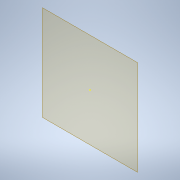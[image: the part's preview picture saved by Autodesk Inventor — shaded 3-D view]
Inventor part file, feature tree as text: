
AUTODESK INVENTOR PART (.ipt)
format: ipt  version: 2020 (Build 240168000, 168)  size: 429,568 bytes
history: native  units: in
note: dims shown in document units (in); Inventor stores cm internally (conversion verified against a paired STEP export)
features: sketch x12, extrude x8, projected_geometry x7, mirror x3, plane x2, other x2, fillet x1, reference x1
ambient origin geometry x8: Origin, YZ Plane, XZ Plane, XY Plane, X Axis, Y Axis, Z Axis, Center Point
bodies: Solid1 (feature_tree)
feature tree (36):
  sketch  "Sketch1"  dims[d0=0.5625in d1=0.0in d2=0.0625in d3=0.0in]
  extrude  "Extrusion1"  Depth=0.0625in TaperAngle=0.0deg
  extrude  "Extrusion2"  Depth=0.125in TaperAngle=0.0deg
  plane  "Work Plane1"
  mirror  "Mirror1"
  fillet  "Fillet1"  Radius=1.375in
  mirror  "Mirror2"
  sketch  "Sketch4"  dims[d12=-0.0625in d13=0.125in d14=0.0in]
  extrude  "Extrusion3"  Depth=1.375in TaperAngle=0.0deg
  extrude  "Extrusion4"  Depth=0.125in TaperAngle=0.0deg
  mirror  "Mirror3"
  extrude  "Extrusion5"  Depth=0.0625in TaperAngle=0.0deg
  sketch  "Sketch8"
  plane  "Work Plane2"
  extrude  "Extrusion6"  [1 undecoded]
  extrude  "Extrusion7"  [1 undecoded]
  sketch  "Sketch11"
  extrude  "Extrusion8"  [1 undecoded]
  sketch  "Sketch2"  dims[d4=0.125in d5=1.375in d6=0.0in d7=1.375in d8=0.0in]
  sketch  "Sketch3"  dims[d9=0.2843in d10=1.375in d11=0.0in]
  sketch  "Sketch5"  dims[d15=0.3125in d16=0.0in d17=0.0625in d18=0.0in]
  sketch  "Sketch6"
  projected_geometry  "Projected Loop1"
  sketch  "Sketch7"
  reference  "Reference1"
  projected_geometry  "Projected Loop2"
  projected_geometry  "Projected Loop3"
  sketch  "Sketch9"
  projected_geometry  "Projected Loop4"
  sketch  "Sketch10"
  projected_geometry  "Projected Loop5"
  sketch  "Sketch12"
  projected_geometry  "Projected Loop6"
  projected_geometry  "Project Cut Edges1"
  other  "Assembly1"
  other  "Micro sized Servo Mount - x4_Simple:1"
note: 3 required parameter values undecoded (feature->parameter linkage not recoverable at this tier; creation-order binding heuristic only, values carry confidence <= 0.55)
